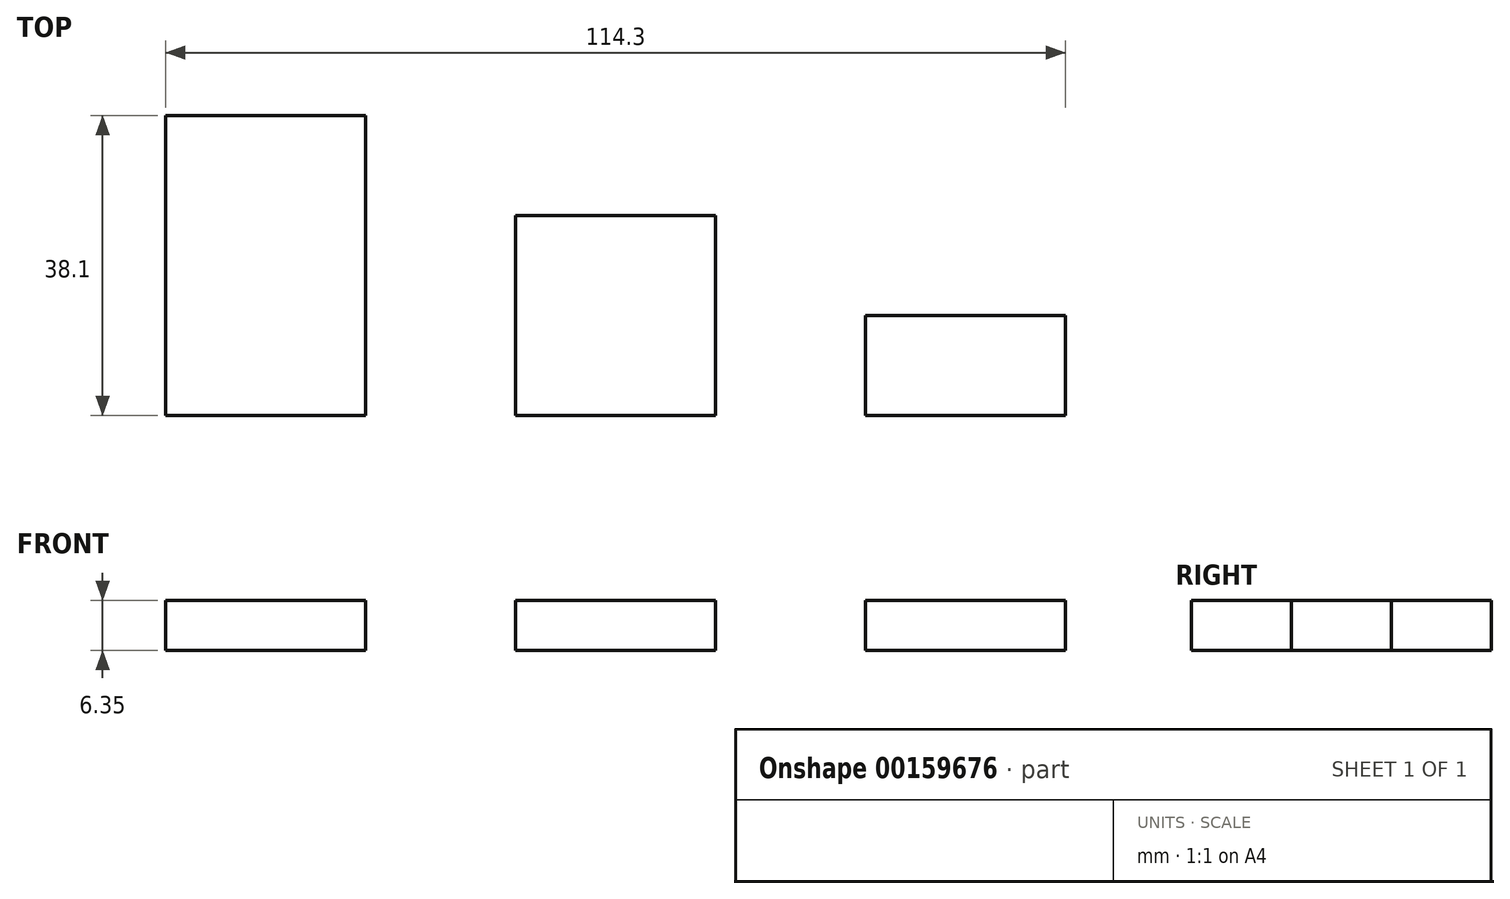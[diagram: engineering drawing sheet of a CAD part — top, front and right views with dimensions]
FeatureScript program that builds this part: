
annotation { "Feature Type Name" : "Feature", "Feature Type Description" : "" }
export const myFeature = defineFeature(function(context is Context, id is Id, definition is map)
    precondition{}
    {
        {
            var Q0;
            Q0=qCreatedBy(makeId("Top.planeOp"),FACE);
            var sketch = newSketch(context, id + "F0", { "sketchPlane" : qUnion([Q0])});
            skLineSegment(sketch, "E0.bottom", {"start": v(0, 0) * mm, "end": v(25.4, 0) * mm});
            skLineSegment(sketch, "E0.top", {"start": v(0, 25.4) * mm, "end": v(25.4, 25.4) * mm});
            skLineSegment(sketch, "E0.left", {"start": v(0, 0) * mm, "end": v(0, 25.4) * mm});
            skLineSegment(sketch, "E0.right", {"start": v(25.4, 0) * mm, "end": v(25.4, 25.4) * mm});
            skLineSegment(sketch, "E1.bottom", {"start": v(44.45, 0) * mm, "end": v(69.85, 0) * mm});
            skLineSegment(sketch, "E1.top", {"start": v(44.45, 12.7) * mm, "end": v(69.85, 12.7) * mm});
            skLineSegment(sketch, "E1.left", {"start": v(44.45, 0) * mm, "end": v(44.45, 12.7) * mm});
            skLineSegment(sketch, "E1.right", {"start": v(69.85, 0) * mm, "end": v(69.85, 12.7) * mm});
            skLineSegment(sketch, "E2.bottom", {"start": v(-19.05, 0) * mm, "end": v(-44.45, 0) * mm});
            skLineSegment(sketch, "E2.top", {"start": v(-19.05, 38.1) * mm, "end": v(-44.45, 38.1) * mm});
            skLineSegment(sketch, "E2.left", {"start": v(-19.05, 0) * mm, "end": v(-19.05, 38.1) * mm});
            skLineSegment(sketch, "E2.right", {"start": v(-44.45, 0) * mm, "end": v(-44.45, 38.1) * mm});
            skSolve(sketch);
        }
        {
            var Q0;
            Q0=makeQuery(id+"F0.imprint","IMPRINT",FACE,{"disambiguationData":[TD([[makeQuery(id+"F0.imprint","IMPRINT",EDGE,{"derivedFrom":sQuery(id+"F0.wireOp",EDGE,"E2.bottom")}),-1.0]])]});
            var Q1;
            Q1=makeQuery(id+"F0.imprint","IMPRINT",FACE,{"disambiguationData":[TD([[makeQuery(id+"F0.imprint","IMPRINT",EDGE,{"derivedFrom":sQuery(id+"F0.wireOp",EDGE,"E0.bottom")}),1.0]])]});
            var Q2;
            Q2=makeQuery(id+"F0.imprint","IMPRINT",FACE,{"disambiguationData":[TD([[makeQuery(id+"F0.imprint","IMPRINT",EDGE,{"derivedFrom":sQuery(id+"F0.wireOp",EDGE,"E1.bottom")}),1.0]])]});
            extrude(context, id + "F1", {"entities" : qUnion([Q0, Q1, Q2]), "depth" : 6.35 * mm});
        }
    });
